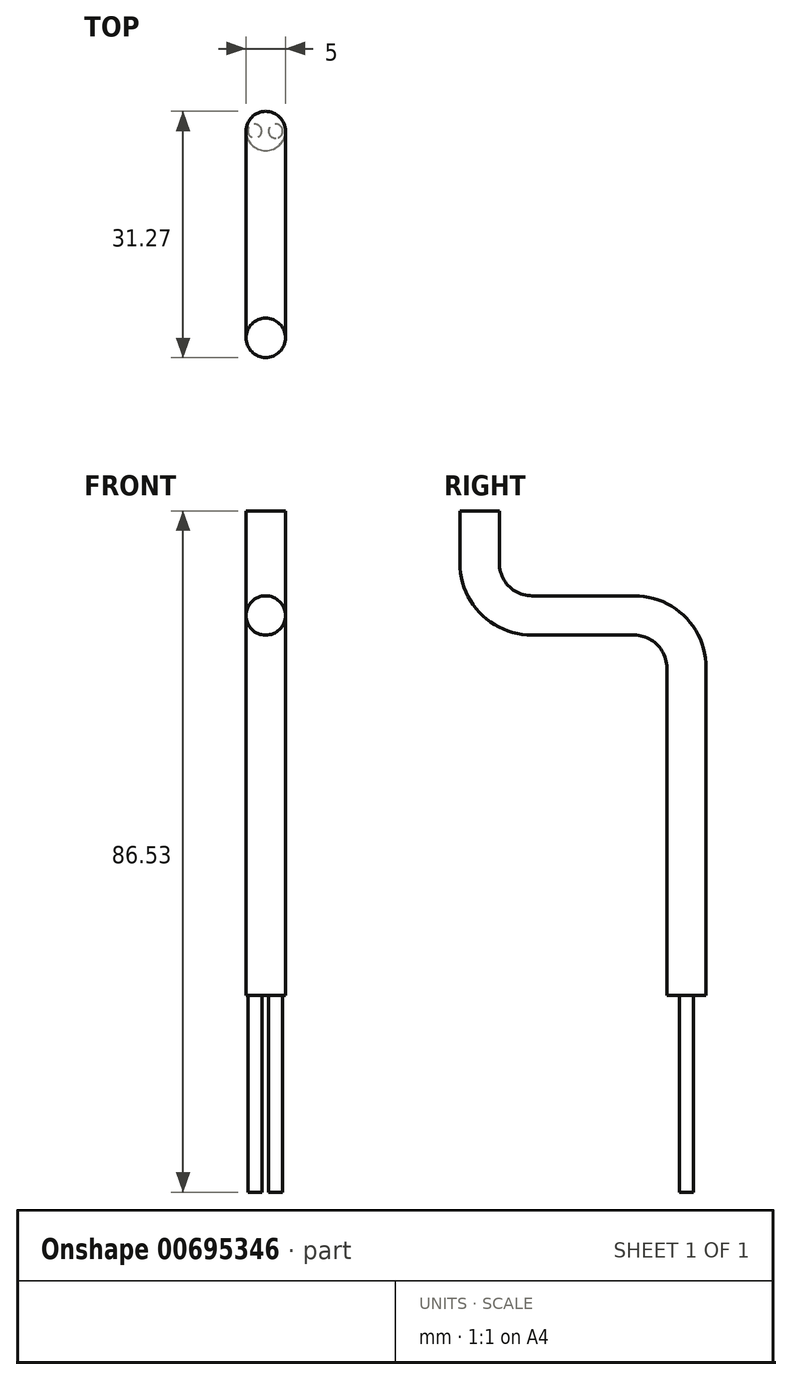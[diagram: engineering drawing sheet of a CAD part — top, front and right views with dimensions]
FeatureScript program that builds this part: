
annotation { "Feature Type Name" : "Feature", "Feature Type Description" : "" }
export const myFeature = defineFeature(function(context is Context, id is Id, definition is map)
    precondition{}
    {
        {
            var Q0;
            Q0=qCreatedBy(makeId("Right.planeOp"),FACE);
            var sketch = newSketch(context, id + "F0", { "sketchPlane" : qUnion([Q0])});
            skLineSegment(sketch, "E0", {"start": v(-19.63, 13.27) * mm, "end": v(-6.63, 13.27) * mm});
            skLineSegment(sketch, "E1", {"start": v(0, 6.63) * mm, "end": v(0, 0) * mm});
            skArc(sketch, "E2", {"start": v(0, 6.63) * mm, "mid": v(-1.94, 11.32) * mm, "end": v(-6.63, 13.27) * mm});
            skLineSegment(sketch, "E3", {"start": v(-26.27, 19.9) * mm, "end": v(-26.27, 26.53) * mm});
            skArc(sketch, "E4", {"start": v(-26.27, 19.9) * mm, "mid": v(-24.32, 15.2) * mm, "end": v(-19.63, 13.27) * mm});
            skSolve(sketch);
        }
        {
            var Q0;
            Q0=qCreatedBy(makeId("Top.planeOp"),FACE);
            var sketch = newSketch(context, id + "F1", { "sketchPlane" : qUnion([Q0])});
            skCircle(sketch, "E5", {"center": v(0, 0) * mm, "radius": 2.5 * mm});
            skSolve(sketch);
        }
        {
            var Q0;
            Q0=makeQuery(id+"F1.imprint","IMPRINT",FACE,{"disambiguationData":[TD([[makeQuery(id+"F1.imprint","IMPRINT",EDGE,{"derivedFrom":sQuery(id+"F1.wireOp",EDGE,"E5")}),1.0]])]});
            var Q1;
            Q1=sQuery(id+"F0.wireOp",EDGE,"E1");
            var Q2;
            Q2=sQuery(id+"F0.wireOp",EDGE,"E2");
            var Q3;
            Q3=sQuery(id+"F0.wireOp",EDGE,"E0");
            var Q4;
            Q4=sQuery(id+"F0.wireOp",EDGE,"E4");
            var Q5;
            Q5=sQuery(id+"F0.wireOp",EDGE,"E3");
            sweep(context, id + "F2", {"profiles" : qUnion([Q0]), "path" : qUnion([Q1, Q2, Q3, Q4, Q5])});
        }
        {
            var Q0;
            Q0 = qSketchRegion(id + "F1", true);
            extrude(context, id + "F3", {"entities" : qUnion([Q0]), "operationType" : NewBodyOperationType.ADD, "oppositeDirection" : true, "depth" : 35 * mm, "offsetDistance" : 25 * mm});
        }
        {
            var Q0;
            Q0=makeQuery(id+"F3.opExtrude","CAP_FACE",FACE,{"disambiguationData":[OSD([sQuery(id+"F1.wireOp",EDGE,"E5")])],"isStart":false});
            var sketch = newSketch(context, id + "F4", { "sketchPlane" : qUnion([Q0])});
            skCircle(sketch, "E6", {"center": v(-1.38, 0) * mm, "radius": 0.88 * mm});
            skCircle(sketch, "E7", {"center": v(1.25, 0) * mm, "radius": 0.9 * mm});
            skSolve(sketch);
        }
        {
            var Q0;
            Q0 = qSketchRegion(id + "F4", true);
            extrude(context, id + "F5", {"entities" : qUnion([Q0]), "operationType" : NewBodyOperationType.ADD, "depth" : 25 * mm, "offsetDistance" : 25 * mm});
        }
    });
